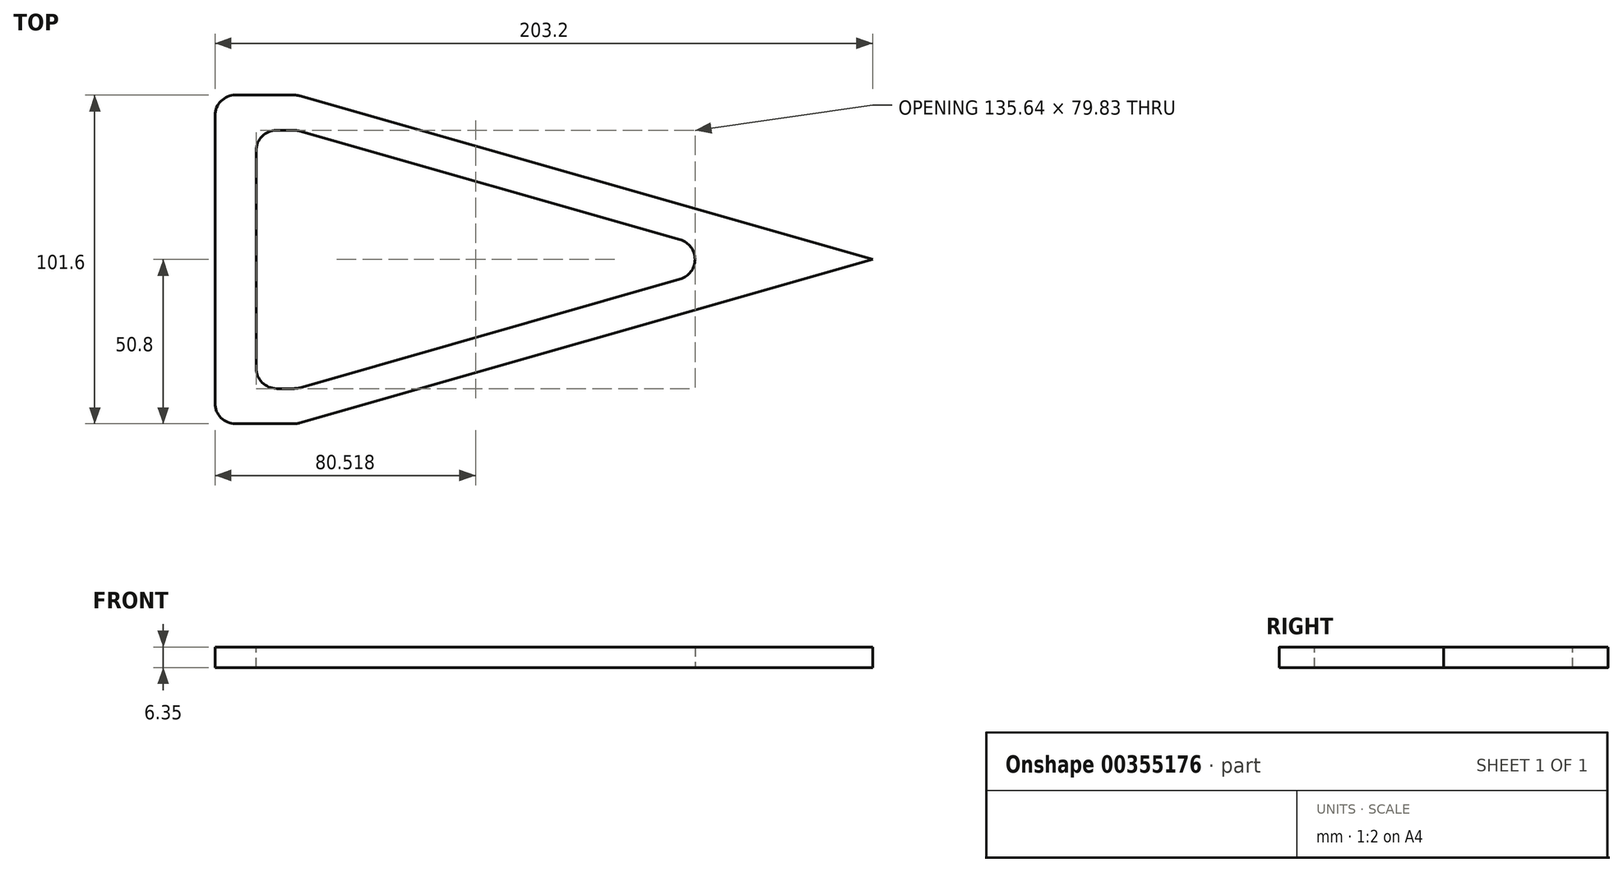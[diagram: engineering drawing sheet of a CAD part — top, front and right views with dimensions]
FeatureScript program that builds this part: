
annotation { "Feature Type Name" : "Feature", "Feature Type Description" : "" }
export const myFeature = defineFeature(function(context is Context, id is Id, definition is map)
    precondition{}
    {
        {
            var Q0;
            Q0=qCreatedBy(makeId("Top.planeOp"),FACE);
            var sketch = newSketch(context, id + "F0", { "sketchPlane" : qUnion([Q0])});
            skLineSegment(sketch, "E0", {"start": v(0, 0) * mm, "end": v(-177.8, 50.8) * mm});
            skLineSegment(sketch, "E1", {"start": v(-177.8, 50.8) * mm, "end": v(-177.8, -50.8) * mm});
            skLineSegment(sketch, "E2", {"start": v(-177.8, -50.8) * mm, "end": v(0, 0) * mm});
            skLineSegment(sketch, "E3", {"start": v(-177.8, 0) * mm, "end": v(0, 0) * mm});
            skLineSegment(sketch, "E4.bottom", {"start": v(-177.8, 50.8) * mm, "end": v(-203.2, 50.8) * mm});
            skLineSegment(sketch, "E4.top", {"start": v(-177.8, -50.8) * mm, "end": v(-203.2, -50.8) * mm});
            skLineSegment(sketch, "E4.right", {"start": v(-203.2, 50.8) * mm, "end": v(-203.2, -50.8) * mm});
            skSolve(sketch);
        }
        {
            var Q0;
            {var subQ0=sQuery(id+"F0.wireOp",EDGE,"E0");Q0=makeQuery(id+"F0.imprint","IMPRINT",FACE,{"disambiguationData":[TD([[makeQuery(id+"F0.imprint","IMPRINT",EDGE,{"derivedFrom":subQ0}),1.0]])]});}
            var Q1;
            {var subQ0=sQuery(id+"F0.wireOp",EDGE,"E2");Q1=makeQuery(id+"F0.imprint","IMPRINT",FACE,{"disambiguationData":[TD([[makeQuery(id+"F0.imprint","IMPRINT",EDGE,{"derivedFrom":subQ0}),1.0]])]});}
            var Q2;
            {var subQ3=sQuery(id+"F0.wireOp",EDGE,"E4.bottom");Q2=makeQuery(id+"F0.imprint","IMPRINT",FACE,{"disambiguationData":[TD([[makeQuery(id+"F0.imprint","IMPRINT",EDGE,{"derivedFrom":subQ3}),1.0]])]});}
            extrude(context, id + "F1", {"entities" : qUnion([Q0, Q1, Q2]), "depth" : 6.35 * mm});
        }
        {
            var Q0;
            Q0=makeQuery(id+"F1.opExtrude","CAP_FACE",FACE,{"disambiguationData":[OSD([sQuery(id+"F0.wireOp",EDGE,"E0"),sQuery(id+"F0.wireOp",EDGE,"E1"),sQuery(id+"F0.wireOp",EDGE,"E2")])],"isStart":false});
            var sketch = newSketch(context, id + "F2", { "sketchPlane" : qUnion([Q0])});
            skLineSegment(sketch, "E5", {"start": v(-177.8, -39.91) * mm, "end": v(-38.1, 0) * mm});
            skLineSegment(sketch, "E6", {"start": v(-38.1, 0) * mm, "end": v(-177.8, 39.91) * mm});
            skPoint(sketch, "E7.oppositeSnap0", {"position": v(-190.5, 50.8) * mm});
            skLineSegment(sketch, "E7.bottom", {"start": v(-177.8, 39.91) * mm, "end": v(-190.5, 39.91) * mm});
            skLineSegment(sketch, "E7.top", {"start": v(-177.8, -39.91) * mm, "end": v(-190.5, -39.91) * mm});
            skLineSegment(sketch, "E7.left", {"start": v(-177.8, 39.91) * mm, "end": v(-177.8, -39.91) * mm});
            skLineSegment(sketch, "E7.right", {"start": v(-190.5, 39.91) * mm, "end": v(-190.5, -39.91) * mm});
            skLineSegment(sketch, "E8", {"start": v(-177.8, 39.91) * mm, "end": v(-177.8, 50.8) * mm});
            skSolve(sketch);
        }
        {
            var Q0;
            Q0 = qSketchRegion(id + "F2", true);
            extrude(context, id + "F3", {"entities" : qUnion([Q0]), "operationType" : NewBodyOperationType.REMOVE, "endBound" : BoundingType.UP_TO_NEXT, "oppositeDirection" : true, "depth" : 25.4 * mm});
        }
        {
            var Q0;
            Q0=makeQuery(id+"F1.opExtrude","SWEPT_EDGE",EDGE,{"disambiguationData":[OSD([sQuery(id+"F0.wireOp",EDGE,"E1"),sQuery(id+"F0.wireOp",EDGE,"E2")])]});
            var Q1;
            Q1=makeQuery(id+"F1.opExtrude","SWEPT_EDGE",EDGE,{"disambiguationData":[OSD([sQuery(id+"F0.wireOp",EDGE,"E0"),sQuery(id+"F0.wireOp",EDGE,"E1")])]});
            var Q2;
            Q2=makeQuery(id+"F1.opExtrude","SWEPT_EDGE",EDGE,{"disambiguationData":[OSD([sQuery(id+"F0.wireOp",EDGE,"E4.top"),sQuery(id+"F0.wireOp",EDGE,"E4.right")])]});
            var Q3;
            Q3=makeQuery(id+"F1.opExtrude","SWEPT_EDGE",EDGE,{"disambiguationData":[OSD([sQuery(id+"F0.wireOp",EDGE,"E4.bottom"),sQuery(id+"F0.wireOp",EDGE,"E4.right")])]});
            fillet(context, id + "F4", {"entities" : qUnion([Q0, Q1, Q2, Q3]), "radius" : 6.35 * mm, "tangentPropagation" : true, "allowEdgeOverflow" : false});
        }
        {
            var Q0;
            Q0=makeQuery(id+"F3.boolean.opBoolean","COPY",EDGE,{"derivedFrom":makeQuery(id+"F3.opExtrude","SWEPT_EDGE",EDGE,{"disambiguationData":[OSD([sQuery(id+"F2.wireOp",EDGE,"G2f1bYyd-QXHx-8MFj-8V2u-q1n4CsCNIkdV"),sQuery(id+"F2.wireOp",EDGE,"E5")])]})});
            var Q1;
            Q1=makeQuery(id+"F3.boolean.opBoolean","COPY",EDGE,{"derivedFrom":makeQuery(id+"F3.opExtrude","SWEPT_EDGE",EDGE,{"disambiguationData":[OSD([sQuery(id+"F2.wireOp",EDGE,"G2f1bYyd-QXHx-8MFj-8V2u-q1n4CsCNIkdV"),sQuery(id+"F2.wireOp",EDGE,"E6")])]})});
            var Q2;
            Q2=makeQuery(id+"F3.boolean.opBoolean","COPY",EDGE,{"derivedFrom":makeQuery(id+"F3.opExtrude","SWEPT_EDGE",EDGE,{"disambiguationData":[OSD([sQuery(id+"F2.wireOp",EDGE,"E5"),sQuery(id+"F2.wireOp",EDGE,"E7.top"),sQuery(id+"F2.wireOp",EDGE,"E7.left")])]})});
            var Q3;
            Q3=makeQuery(id+"F3.boolean.opBoolean","COPY",EDGE,{"derivedFrom":makeQuery(id+"F3.opExtrude","SWEPT_EDGE",EDGE,{"disambiguationData":[OSD([sQuery(id+"F2.wireOp",EDGE,"E7.top"),sQuery(id+"F2.wireOp",EDGE,"E7.right")])]})});
            var Q4;
            Q4=makeQuery(id+"F3.boolean.opBoolean","COPY",EDGE,{"derivedFrom":makeQuery(id+"F3.opExtrude","SWEPT_EDGE",EDGE,{"disambiguationData":[OSD([sQuery(id+"F2.wireOp",EDGE,"E7.bottom"),sQuery(id+"F2.wireOp",EDGE,"E7.right")])]})});
            var Q5;
            Q5=makeQuery(id+"F3.boolean.opBoolean","COPY",EDGE,{"derivedFrom":makeQuery(id+"F3.opExtrude","SWEPT_EDGE",EDGE,{"disambiguationData":[OSD([sQuery(id+"F2.wireOp",EDGE,"E6"),sQuery(id+"F2.wireOp",EDGE,"E7.bottom"),sQuery(id+"F2.wireOp",EDGE,"E7.left")])]})});
            fillet(context, id + "F5", {"entities" : qUnion([Q0, Q1, Q2, Q3, Q4, Q5]), "radius" : 6.35 * mm, "tangentPropagation" : true, "allowEdgeOverflow" : false});
        }
    });
